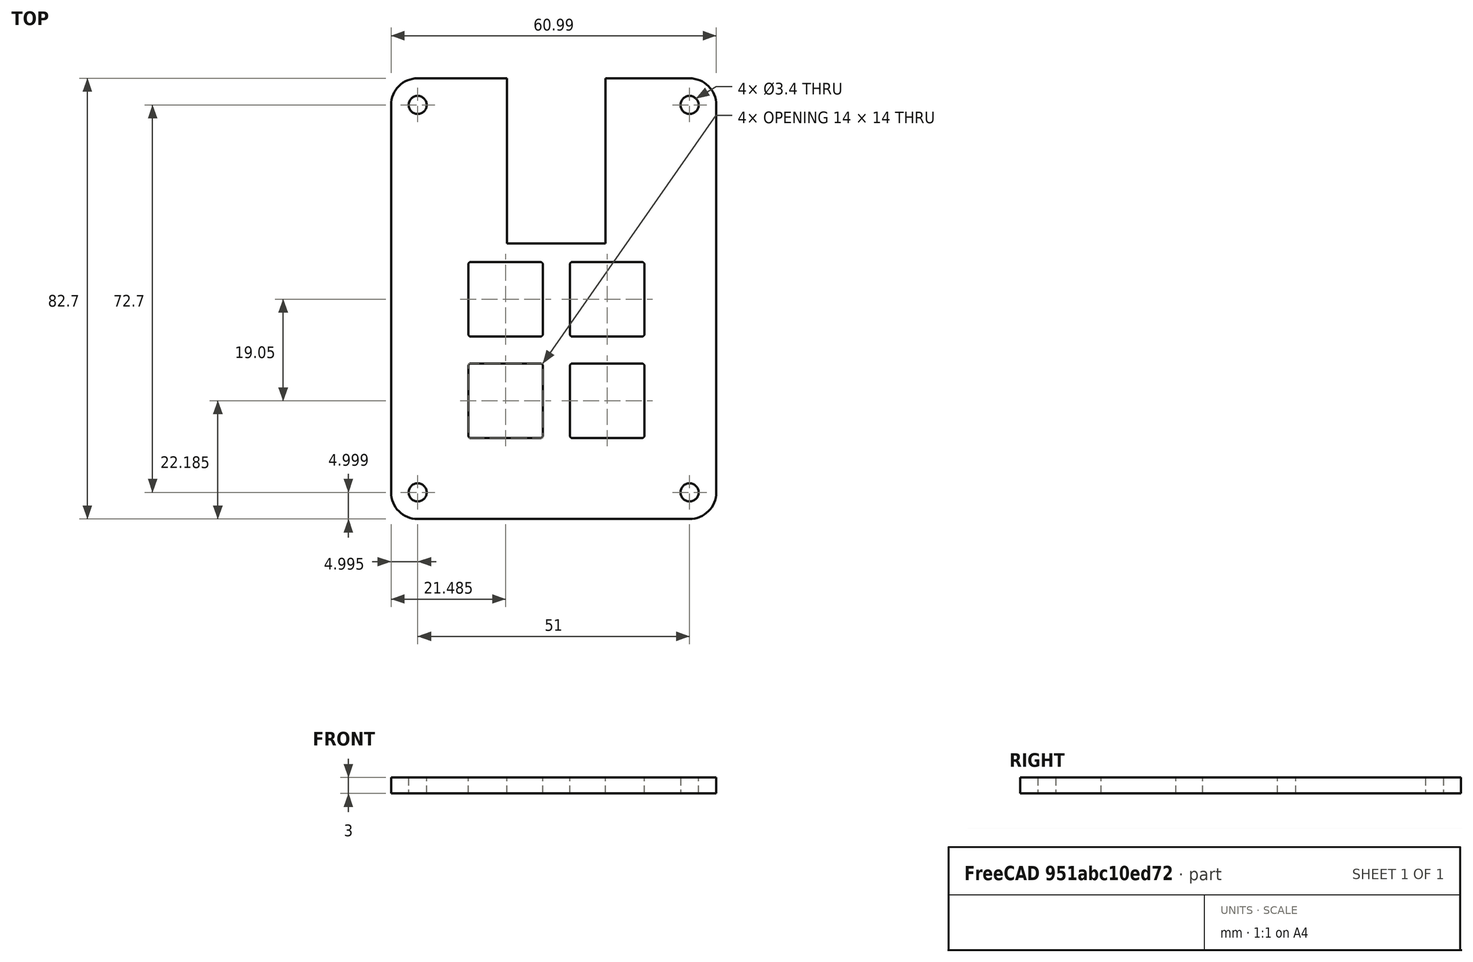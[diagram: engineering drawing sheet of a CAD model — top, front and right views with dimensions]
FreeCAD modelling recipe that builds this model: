
FCSTD DOCUMENT  (FreeCAD 1.0R39109 (Git))
Label: Plate
License: All rights reserved
LicenseURL: https://en.wikipedia.org/wiki/All_rights_reserved
objects: Sketcher::SketchObject×2, PartDesign::Pad×1, PartDesign::Pocket×1, PartDesign::Body×1
note: 11 computed .brp shape members not serialized (recipe doc carries the construction recipe); baked Part::Feature solids carry a one-line shape summary decoded from their .brp

FEATURE [Sketcher::SketchObject] Sketch
  ArcFitTolerance = 1e-06
  FullyConstrained = false
  MakeInternals = false
  sketch-geometry (32):
    g0: LineSegment StartX=3.025 StartY=-2.525 StartZ=0 EndX=16.025 EndY=-2.525 EndZ=0
    g1: LineSegment StartX=3.025 StartY=-16.525 StartZ=0 EndX=16.025 EndY=-16.525 EndZ=0
    g2: LineSegment StartX=2.525 StartY=-3.025 StartZ=0 EndX=2.525 EndY=-16.025 EndZ=0
    g3: LineSegment StartX=16.525 StartY=-3.025 StartZ=0 EndX=16.525 EndY=-16.025 EndZ=0
    g4: ArcOfCircle CenterX=3.025 CenterY=-3.025 CenterZ=0 NormalX=0 NormalY=0 NormalZ=1 AngleXU=0 Radius=0.5 StartAngle=1.5708 EndAngle=3.14159
    g5: ArcOfCircle CenterX=16.025 CenterY=-3.025 CenterZ=0 NormalX=0 NormalY=0 NormalZ=1 AngleXU=0 Radius=0.5 StartAngle=0 EndAngle=1.5708
    g6: ArcOfCircle CenterX=3.025 CenterY=-16.025 CenterZ=0 NormalX=0 NormalY=0 NormalZ=1 AngleXU=0 Radius=0.5 StartAngle=3.14159 EndAngle=4.71239
    g7: ArcOfCircle CenterX=16.025 CenterY=-16.025 CenterZ=0 NormalX=0 NormalY=0 NormalZ=1 AngleXU=0 Radius=0.5 StartAngle=4.71239 EndAngle=6.28319
    g8: LineSegment StartX=22.075 StartY=-2.525 StartZ=0 EndX=35.075 EndY=-2.525 EndZ=0
    g9: LineSegment StartX=22.075 StartY=-16.525 StartZ=0 EndX=35.075 EndY=-16.525 EndZ=0
    g10: LineSegment StartX=21.575 StartY=-3.025 StartZ=0 EndX=21.575 EndY=-16.025 EndZ=0
    g11: LineSegment StartX=35.575 StartY=-3.025 StartZ=0 EndX=35.575 EndY=-16.025 EndZ=0
    g12: ArcOfCircle CenterX=22.075 CenterY=-3.025 CenterZ=0 NormalX=0 NormalY=0 NormalZ=1 AngleXU=0 Radius=0.5 StartAngle=1.5708 EndAngle=3.14159
    g13: ArcOfCircle CenterX=35.075 CenterY=-3.025 CenterZ=0 NormalX=0 NormalY=0 NormalZ=1 AngleXU=0 Radius=0.5 StartAngle=0 EndAngle=1.5708
    g14: ArcOfCircle CenterX=22.075 CenterY=-16.025 CenterZ=0 NormalX=0 NormalY=0 NormalZ=1 AngleXU=0 Radius=0.5 StartAngle=3.14159 EndAngle=4.71239
    g15: ArcOfCircle CenterX=35.075 CenterY=-16.025 CenterZ=0 NormalX=0 NormalY=0 NormalZ=1 AngleXU=0 Radius=0.5 StartAngle=4.71239 EndAngle=6.28319
    g16: LineSegment StartX=3.025 StartY=-21.575 StartZ=0 EndX=16.025 EndY=-21.575 EndZ=0
    g17: LineSegment StartX=3.025 StartY=-35.575 StartZ=0 EndX=16.025 EndY=-35.575 EndZ=0
    g18: LineSegment StartX=2.525 StartY=-22.075 StartZ=0 EndX=2.525 EndY=-35.075 EndZ=0
    g19: LineSegment StartX=16.525 StartY=-22.075 StartZ=0 EndX=16.525 EndY=-35.075 EndZ=0
    g20: ArcOfCircle CenterX=3.025 CenterY=-22.075 CenterZ=0 NormalX=0 NormalY=0 NormalZ=1 AngleXU=0 Radius=0.5 StartAngle=1.5708 EndAngle=3.14159
    g21: ArcOfCircle CenterX=16.025 CenterY=-22.075 CenterZ=0 NormalX=0 NormalY=0 NormalZ=1 AngleXU=0 Radius=0.5 StartAngle=0 EndAngle=1.5708
    g22: ArcOfCircle CenterX=3.025 CenterY=-35.075 CenterZ=0 NormalX=0 NormalY=0 NormalZ=1 AngleXU=0 Radius=0.5 StartAngle=3.14159 EndAngle=4.71239
    g23: ArcOfCircle CenterX=16.025 CenterY=-35.075 CenterZ=0 NormalX=0 NormalY=0 NormalZ=1 AngleXU=0 Radius=0.5 StartAngle=4.71239 EndAngle=6.28319
    g24: LineSegment StartX=22.075 StartY=-21.575 StartZ=0 EndX=35.075 EndY=-21.575 EndZ=0
    g25: LineSegment StartX=22.075 StartY=-35.575 StartZ=0 EndX=35.075 EndY=-35.575 EndZ=0
    g26: LineSegment StartX=21.575 StartY=-22.075 StartZ=0 EndX=21.575 EndY=-35.075 EndZ=0
    g27: LineSegment StartX=35.575 StartY=-22.075 StartZ=0 EndX=35.575 EndY=-35.075 EndZ=0
    g28: ArcOfCircle CenterX=22.075 CenterY=-22.075 CenterZ=0 NormalX=0 NormalY=0 NormalZ=1 AngleXU=0 Radius=0.5 StartAngle=1.5708 EndAngle=3.14159
    g29: ArcOfCircle CenterX=35.075 CenterY=-22.075 CenterZ=0 NormalX=0 NormalY=0 NormalZ=1 AngleXU=0 Radius=0.5 StartAngle=0 EndAngle=1.5708
    g30: ArcOfCircle CenterX=22.075 CenterY=-35.075 CenterZ=0 NormalX=0 NormalY=0 NormalZ=1 AngleXU=0 Radius=0.5 StartAngle=3.14159 EndAngle=4.71239
    g31: ArcOfCircle CenterX=35.075 CenterY=-35.075 CenterZ=0 NormalX=0 NormalY=0 NormalZ=1 AngleXU=0 Radius=0.5 StartAngle=4.71239 EndAngle=6.28319
  constraints (32):
    c: Coincident(g18,g22)
    c: Coincident(g18,g20)
    c: Coincident(g2,g6)
    c: Coincident(g2,g4)
    c: Coincident(g17,g22)
    c: Coincident(g16,g20)
    c: Coincident(g1,g6)
    c: Coincident(g0,g4)
    c: Coincident(g17,g23)
    c: Coincident(g16,g21)
    c: Coincident(g1,g7)
    c: Coincident(g0,g5)
    c: Coincident(g19,g23)
    c: Coincident(g19,g21)
    c: Coincident(g3,g7)
    c: Coincident(g3,g5)
    c: Coincident(g26,g30)
    c: Coincident(g26,g28)
    c: Coincident(g10,g14)
    c: Coincident(g10,g12)
    c: Coincident(g25,g30)
    c: Coincident(g24,g28)
    c: Coincident(g9,g14)
    c: Coincident(g8,g12)
    c: Coincident(g25,g31)
    c: Coincident(g24,g29)
    c: Coincident(g9,g15)
    c: Coincident(g8,g13)
    c: Coincident(g27,g31)
    c: Coincident(g27,g29)
    c: Coincident(g11,g15)
    c: Coincident(g11,g13)
FEATURE [Sketcher::SketchObject] Sketch001
  ArcFitTolerance = 1e-06
  AttachmentSupport = -> [XY_Plane]
  ExternalGeometry = -> [Sketch]
  FullyConstrained = false
  MakeInternals = false
  MapMode = 5
  sketch-geometry (18):
    g0: LineSegment StartX=-11.965 StartY=26.939 StartZ=0 EndX=-11.965 EndY=-45.761 EndZ=0
    g1: LineSegment StartX=-6.965 StartY=-50.761 StartZ=0 EndX=44.035 EndY=-50.761 EndZ=0
    g2: LineSegment StartX=49.035 StartY=-45.761 StartZ=0 EndX=49.035 EndY=26.939 EndZ=0
    g3: LineSegment StartX=44.035 StartY=31.939 StartZ=0 EndX=28.285 EndY=31.939 EndZ=0
    g4: ArcOfCircle CenterX=-6.965 CenterY=26.939 CenterZ=0 NormalX=0 NormalY=0 NormalZ=1 AngleXU=0 Radius=5 StartAngle=1.5708 EndAngle=3.14159
    g5: ArcOfCircle CenterX=-6.965 CenterY=-45.761 CenterZ=0 NormalX=0 NormalY=0 NormalZ=1 AngleXU=0 Radius=5 StartAngle=3.14159 EndAngle=4.71239
    g6: ArcOfCircle CenterX=44.035 CenterY=-45.761 CenterZ=0 NormalX=0 NormalY=0 NormalZ=1 AngleXU=0 Radius=5 StartAngle=4.71239 EndAngle=6.28319
    g7: ArcOfCircle CenterX=44.035 CenterY=26.939 CenterZ=0 NormalX=0 NormalY=0 NormalZ=1 AngleXU=0 Radius=5 StartAngle=0 EndAngle=1.5708
    g8: GeomPoint [constr] X=-11.965 Y=31.939 Z=0
    g9: GeomPoint [constr] X=49.035 Y=-50.761 Z=0
    g10: Circle CenterX=-6.965 CenterY=-45.761 CenterZ=0 NormalX=0 NormalY=0 NormalZ=1 AngleXU=0 Radius=1.7
    g11: Circle CenterX=44.035 CenterY=-45.761 CenterZ=0 NormalX=0 NormalY=0 NormalZ=1 AngleXU=0 Radius=1.7
    g12: Circle CenterX=44.035 CenterY=26.939 CenterZ=0 NormalX=0 NormalY=0 NormalZ=1 AngleXU=0 Radius=1.7
    g13: Circle CenterX=-6.965 CenterY=26.939 CenterZ=0 NormalX=0 NormalY=0 NormalZ=1 AngleXU=0 Radius=1.7
    g14: LineSegment StartX=9.785 StartY=31.939 StartZ=0 EndX=9.785 EndY=0.939 EndZ=0
    g15: LineSegment StartX=9.785 StartY=0.939 StartZ=0 EndX=28.285 EndY=0.939 EndZ=0
    g16: LineSegment StartX=28.285 StartY=0.939 StartZ=0 EndX=28.285 EndY=31.939 EndZ=0
    g17: LineSegment StartX=9.785 StartY=31.939 StartZ=0 EndX=-6.965 EndY=31.939 EndZ=0
  constraints (47):
    c: Tangent(g0,g4) = -1.5708
    c: Tangent(g0,g5) = -1.5708
    c: Tangent(g1,g5) = -1.5708
    c: Tangent(g1,g6) = -1.5708
    c: Tangent(g2,g6) = -1.5708
    c: Tangent(g2,g7) = -1.5708
    c: Tangent(g3,g7) = -1.5708
    c: Coincident(g17,g4) = -1.5708
    c: Vertical(g0)
    c: Vertical(g2)
    c: Horizontal(g1)
    c: Horizontal(g3)
    c: Equal(g4,g5)
    c: Equal(g5,g6)
    c: Equal(g6,g7)
    c: PointOnObject(g8,g0)
    c: PointOnObject(g8,g17)
    c: PointOnObject(g9,g1)
    c: PointOnObject(g9,g2)
    c: Radius(g5) = 5
    c: DistanceX(g17,g3) = 51
    c: DistanceY(g2,g2) = 72.7
    c: Diameter(g10) = 3.4
    c: Diameter(g11) = 3.4
    c: Diameter(g12) = 3.4
    c: Diameter(g13) = 3.4
    c: Distance(g13,g0) = 5
    c: Distance(g13,g3) = 5
    c: Distance(g12,g2) = 5
    c: Distance(g12,g3) = 5
    c: Distance(g11,g2) = 5
    c: Distance(g11,g1) = 5
    c: Distance(g10,g0) = 5
    c: Distance(g10,g1) = 5
    c: Distance(g1,g-4) = 15.186
    c: Distance(g0,g-3) = 14.49
    c: Coincident(g14,g15)
    c: Coincident(g15,g16)
    c: Vertical(g14)
    c: Vertical(g16)
    c: Horizontal(g15)
    c: Distance(g14,g16) = 18.5
    c: Distance(g15,g14) = 31
    c: PointOnObject(g14,g17)
    c: Distance(g0,g14) = 21.75
    c: PointOnObject(g3,g16)
    c: PointOnObject(g17,g14)
FEATURE [PartDesign::Pad] Pad
  Direction = (0,0,1)
  Length = 3
  Length2 = 10
  Profile = -> Sketch001
  ReferenceAxis = -> Sketch001 [N_Axis]
  Refine = true
  Suppressed = false
  Type = 0
FEATURE [PartDesign::Pocket] Pocket
  BaseFeature = -> Pad
  Direction = (0,0,-1)
  Length = 10
  Length2 = 5
  Profile = -> Sketch
  ReferenceAxis = -> Sketch [N_Axis]
  Refine = true
  Reversed = true
  Suppressed = false
  Type = 0
FEATURE [PartDesign::Body] Body
  AllowCompound = false
  Group = -> [Sketch001,Sketch,Pad,Pocket]
  Origin = -> Origin
  Tip = -> Pocket
